# Revit family: TRH-242410
name_source: partatom
category: Plumbing Fixtures
revit_build: Autodesk Revit MEP 2016 (Build: 20150220_1215(x64)
units: mm (PartAtom-declared; Revit-internal decimal feet)

## family parameters
Cut with Voids When Loaded = No
Host = Face
OmniClass Number = 23.45.05.21.14.17
OmniClass Title = Sanitary Disposal Connectors
Part Type = Normal
Room Calculation Point = No
Round Connector Dimension = Use Diameter
Shared = Yes

## types (1)
- TRH-242410
    Amperage = 0
    CW Connection = No
    Default Elevation = 0"
    Description = Terrazzo Reduced Height Mop Sink
    HW Connection = No
    Manufacturer = Acorn Engineering Co.
    Material = Type 304 Stainless Steel
    Model = TRH-242410
    Revised Date = 04/17/17
    TRH-242410- Terrazzo Reduced Height Mop Sink = Yes
    Tempered Water Connection = No
    URL = https://www.acorneng.com
    Vent Connection = No
    Voltage = 0
    Waste Connection = Yes

## geometry (parser evidence)
native form markers: Sweep x5
no freeform markers — native parametric forms only
